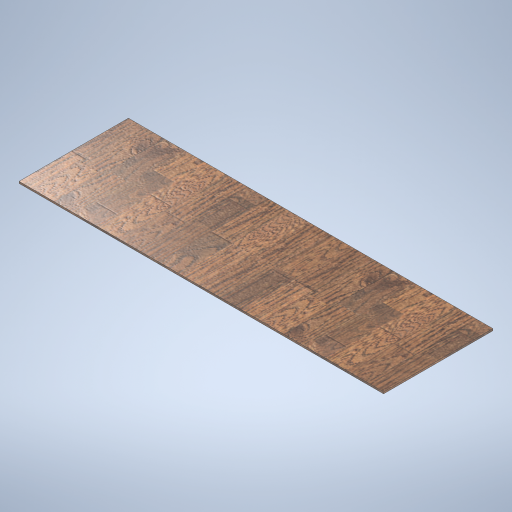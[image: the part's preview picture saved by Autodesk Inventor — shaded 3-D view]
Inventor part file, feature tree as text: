
AUTODESK INVENTOR PART (.ipt)
format: ipt  version: 2023 (Build 270158030, 158C)  size: 357,888 bytes
history: native  units: mm
features: extrude x1, sketch x1
ambient origin geometry x8: Origin, YZ Plane, XZ Plane, XY Plane, X Axis, Y Axis, Z Axis, Center Point
bodies: Solid1 (feature_tree)
feature tree (2):
  extrude  "Extrusion1"  Depth=300.0mm
  sketch  "Sketch1"  dims[d0=1000.0mm d1=300.0mm d2=5.0mm d3=0.0mm]
